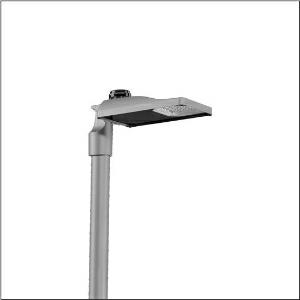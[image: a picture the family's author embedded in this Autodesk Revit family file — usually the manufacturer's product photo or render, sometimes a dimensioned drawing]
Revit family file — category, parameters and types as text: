
# Revit family: streetlight_sl_31_micro___p1_0a_5xh1a7bn08da_f975
name_source: partatom
category: Lighting Fixtures
units: mm (PartAtom-declared; Revit-internal decimal feet)

## family parameters
Cut with Voids When Loaded = No
Host = Face
Light Source = No
Part Type = Normal
Room Calculation Point = No
Round Connector Dimension = Use Diameter
Shared = No

## types (1)
- --- (1 x LED, 3700 lm, 35.5 W, 2200K)
    Apparent Load = 36 VA
    CIE Flux Codes = 23 55 94 100 100
    Color Rendering = 70
    Color Temperature = 2200K
    Default Elevation = 1800 mm
    Description = Streetlight SL 31 micro NEMA (7pin) mast luminaire for post-top, side-entry; light control with lens of PMMA; light distribution: P1.0a, direct asymmetric distribution, for standard-compliant lighting for roads and squares; LED: luminous flux: 3.700lm, light colour: 722, colour temperature: 2200K; luminous efficacy: 104,2lm/W; control: overheat protection, intelligent temperature release in ECG and LED module, constant luminous flux control, time-dependent luminous flux control, flexible luminous flux parameterisation, pre-setting: linear dimming characteristic; luminaire housing, of diecast aluminium, Siteco® metallic grey (DB 702S), corrosivity category C5 high according to DIN EN ISO 12944; cover of toughened safety glass, transparent, mast flange of diecast aluminium, Siteco® metallic grey (DB 702S), spigot size: 76/60mm, mast flange included unmounted; with cable H07RN-F 3x 1.5mm², cable length: 6,5m, connection cable pre-assembled; mains connection: 220..240V, AC, 50/60Hz; power consumption (at start of service life): 35,5W / (at end of service life): 37,5W / (with reduced operation 50%): 15,4W; protection rating (complete): IP66; insulation class (complete): insulation class I (protective earthing); impact resistance: IK10; certification: CE, ENEC, ENEC+, VDE, UKCA; permissible operating ambient temperature for outdoor applications: -40..+50°C; packaging unit: 1 piece

Light Distribution: P1.0a
    Height = 76 mm
    Lamp = 1 x LED
    Lamp Light Flux = 3700 lm
    Lamp Power = 35.5 W
    Lamp count = 1
    Length = 467 mm
    Luminous efficacy = 104 lm/W
    Manufacturer = Siteco
    ModVariant = No
    Model = 5XH1A7BN08DA
    Number of Poles = 1
    OnlyDefault = Yes
    Power Factor = 1
    Product Name = Streetlight SL 31 micro | P1.0a
    Product group = mast luminaire | pylon top
    ProductGroupID = 6100
    Protection Class = Protection class I
    Protection Degree = IP 66
    RLX_Detail_Level = 1
    RLX_Emergency_Light_Flux = 0 lm
    RLX_Emergency_Type = 0
    RLX_Emergency_Type_DB = No
    RlxData = <blob elided: 23337 chars, md5=6f45834b>
    Socket = socket
    Standby Power = 0 W
    System Light Flux = 3700 lm
    System Power = 36 W
    Type Comments = factory setting: luminous flux: 100 % | dim-lin: 254 | 700 mA
    Type Image = l_1300305.jpg
    URL = http://relux.com
    VarID = @adj_014789
    Voltage = 0 V
    Weight = 0.00 kg
    Width = 265 mm

## geometry (parser evidence)
native form markers: Blend x4, Sweep x9
no freeform markers — native parametric forms only
